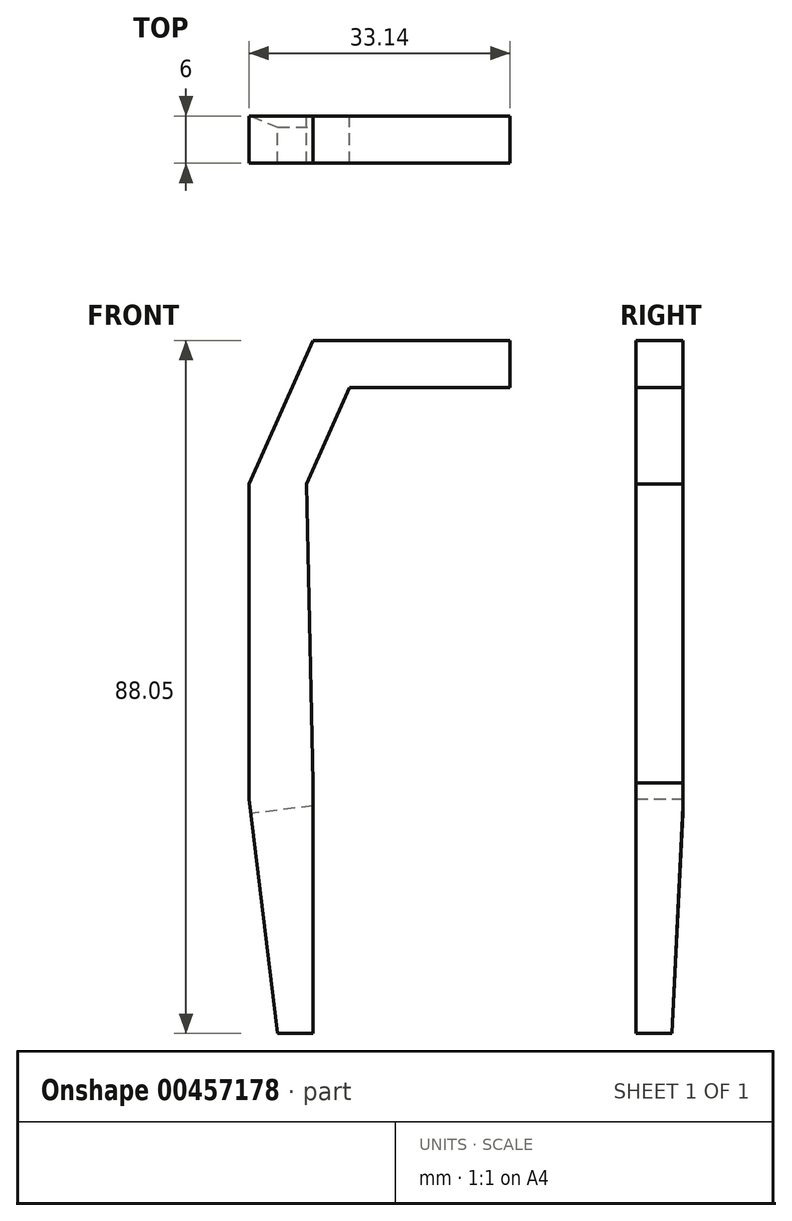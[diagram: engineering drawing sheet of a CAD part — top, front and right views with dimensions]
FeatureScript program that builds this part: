
annotation { "Feature Type Name" : "Feature", "Feature Type Description" : "" }
export const myFeature = defineFeature(function(context is Context, id is Id, definition is map)
    precondition{}
    {
        {
            var Q0;
            Q0=qCreatedBy(makeId("Front.planeOp"),FACE);
            var sketch = newSketch(context, id + "F0", { "sketchPlane" : qUnion([Q0])});
            skLineSegment(sketch, "E0", {"start": v(0, -31.83) * mm, "end": v(-4.5, -31.83) * mm});
            skLineSegment(sketch, "E1", {"start": v(-4.5, -31.83) * mm, "end": v(-8.14, -2.05) * mm});
            skLineSegment(sketch, "E2", {"start": v(-8.14, -2.05) * mm, "end": v(-8.14, 37.95) * mm});
            skLineSegment(sketch, "E3", {"start": v(-8.14, 37.95) * mm, "end": v(0, 56.22) * mm});
            skLineSegment(sketch, "E4", {"start": v(0, 56.22) * mm, "end": v(25, 56.22) * mm});
            skLineSegment(sketch, "E5", {"start": v(25, 56.22) * mm, "end": v(25, 50.22) * mm});
            skLineSegment(sketch, "E6", {"start": v(25, 50.22) * mm, "end": v(4.64, 50.22) * mm});
            skLineSegment(sketch, "E7", {"start": v(4.64, 50.22) * mm, "end": v(-0.82, 37.95) * mm});
            skLineSegment(sketch, "E8", {"start": v(-0.82, 37.95) * mm, "end": v(0, 0) * mm});
            skLineSegment(sketch, "E9", {"start": v(0, 0) * mm, "end": v(0, -31.83) * mm});
            skSolve(sketch);
        }
        {
            var Q0;
            Q0 = qSketchRegion(id + "F0", true);
            extrude(context, id + "F1", {"entities" : qUnion([Q0]), "depth" : 6 * mm});
        }
        {
            var Q0;
            Q0=makeQuery(id+"F1.opExtrude","SWEPT_FACE",FACE,{"disambiguationData":[OSD([sQuery(id+"F0.wireOp",EDGE,"E1")])]});
            var sketch = newSketch(context, id + "F2", { "sketchPlane" : qUnion([Q0])});
            skLineSegment(sketch, "E10", {"start": v(0, -2.9) * mm, "end": v(1.54, -33.72) * mm});
            skLineSegment(sketch, "E11", {"start": v(1.54, -33.72) * mm, "end": v(-1.35, -33.87) * mm});
            skLineSegment(sketch, "E12", {"start": v(-1.35, -33.87) * mm, "end": v(0, -2.9) * mm});
            skSolve(sketch);
        }
        {
            var Q0;
            Q0 = qSketchRegion(id + "F2", true);
            extrude(context, id + "F3", {"entities" : qUnion([Q0]), "operationType" : NewBodyOperationType.REMOVE, "oppositeDirection" : true, "depth" : 25 * mm});
        }
    });
